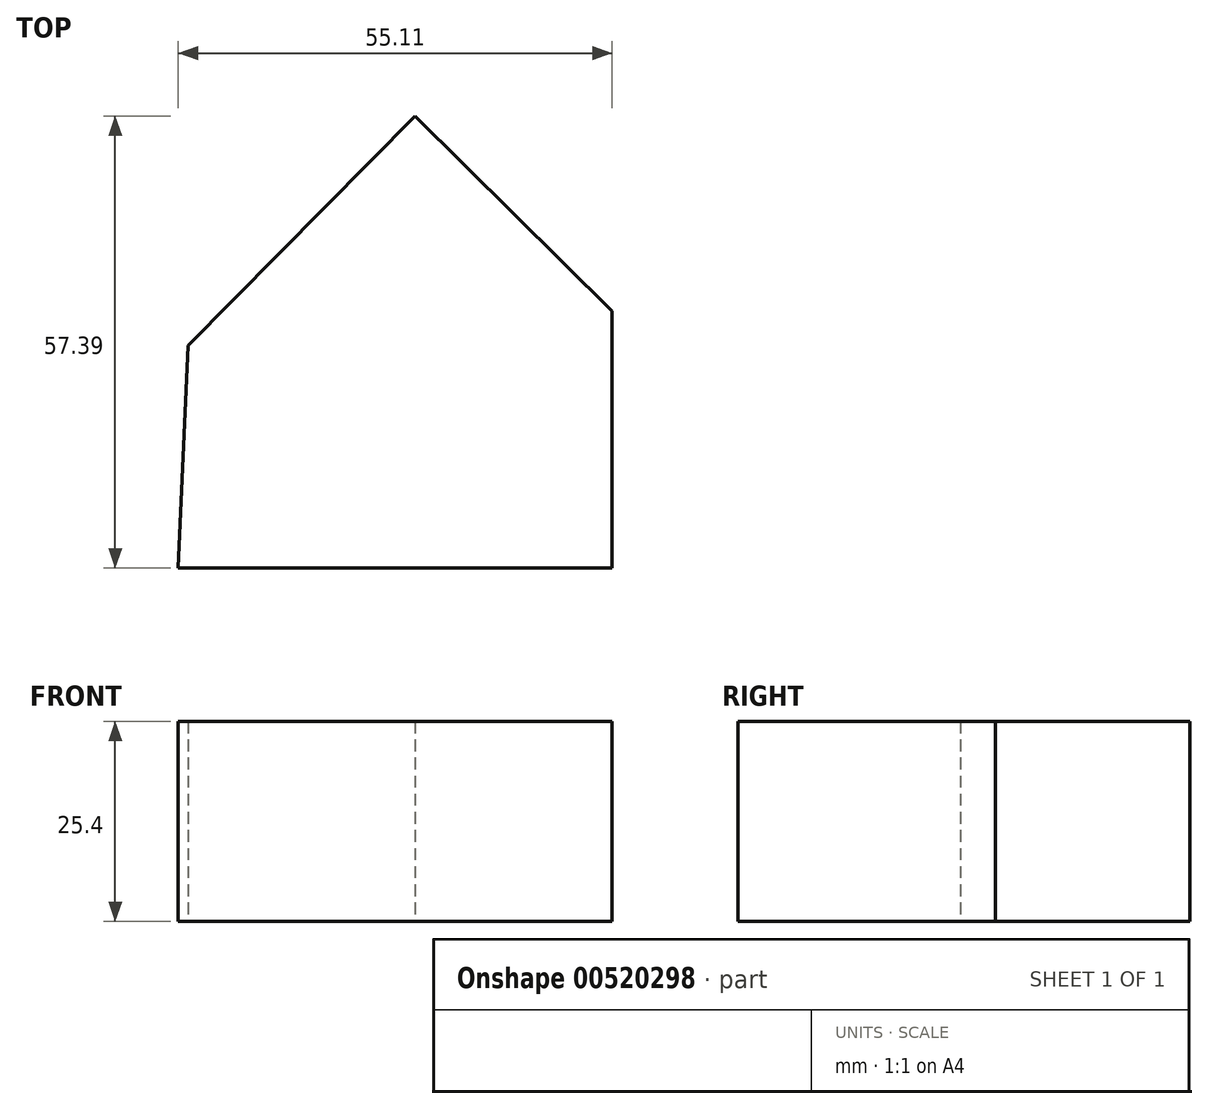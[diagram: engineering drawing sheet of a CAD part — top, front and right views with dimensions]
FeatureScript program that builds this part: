
annotation { "Feature Type Name" : "Feature", "Feature Type Description" : "" }
export const myFeature = defineFeature(function(context is Context, id is Id, definition is map)
    precondition{}
    {
        {
            var Q0;
            Q0=qCreatedBy(makeId("Top.planeOp"),FACE);
            var sketch = newSketch(context, id + "F0", { "sketchPlane" : qUnion([Q0])});
            skLineSegment(sketch, "E0", {"start": v(-28.79, 40.8) * mm, "end": v(0, 69.95) * mm});
            skLineSegment(sketch, "E1", {"start": v(0, 69.95) * mm, "end": v(25.05, 45.22) * mm});
            skLineSegment(sketch, "E2", {"start": v(25.05, 45.22) * mm, "end": v(25.05, 12.56) * mm});
            skLineSegment(sketch, "E3", {"start": v(25.05, 12.56) * mm, "end": v(-30.06, 12.56) * mm});
            skLineSegment(sketch, "E4", {"start": v(-30.06, 12.56) * mm, "end": v(-28.79, 40.8) * mm});
            skSolve(sketch);
        }
        {
            var Q0;
            Q0=makeQuery(id+"F0.imprint","IMPRINT",FACE,{"disambiguationData":[TD([[makeQuery(id+"F0.imprint","IMPRINT",EDGE,{"derivedFrom":sQuery(id+"F0.wireOp",EDGE,"E0")}),-1.0]])]});
            extrude(context, id + "F1", {"entities" : qUnion([Q0]), "depth" : 25.4 * mm, "offsetDistance" : 25.4 * mm});
        }
    });
